# Revit family: Domotics-DomesticRanges-GEWISS-CHORUS_PROTECTION-ONE-WAY_SWITCH_MCB
name_source: partatom
category: Apparecchi elettrici
revit_build: Autodesk Revit 2016 (Build: 20161004_0715(x64)
units: mm (PartAtom-declared; Revit-internal decimal feet)

## family parameters
Condiviso = Sì
Host = Superficie
Mantenere orientamento annotazione = Sì
Punto di calcolo locali = Sì
Quota connettore circolare = Usa diametro
Taglio con vuoti quando caricato = Sì
Tipo di parte = Normale

## types (18) — shared parameters
Breaking capacity = 3KA
Carico apparente = 0 VA
Catalogue = DOMOTICS
Catalogue Range = CHORUS - DOMESTIC RANGE
Curve = C
Electrocod = 0131
IDF = 0539b41e-61ac-4be8-8c77-aad5fbf7d169
IDT = 300d05bc-7aec-4f69-9cb1-967f6c419845
Immagine tipo = GW14461.jpg
N. poli = 1
No. Chorus modules = 1
No. Chorus modules: = 1
Produttore = GEWISS S.p.A.
Prospetto di default = 1219 mm
SEO = MCB
Technical sheet = https://www.gewiss.com
Tipo_ = CHORUS INT MAGNETOTERMICO_GENERICO : TITANIO
Type = MCB
URL = https://www.gewiss.com
Version file RFA = 19.0
Volt = 230 V
Voltage = 230V ac
Voltage: = 230V ac

## per-type parameters (varying)
| type | Colour | Description. | Description: | Descrizione | EAN code | Modello | Rated current (A) | Rated current (In) |
| GW12462 - MCB 1P C10 3kA 230V ac 1M Black | Black | One-way switch (1P) | Single pole (1P) | MCB 1P C10 3KA 230V AC 1M BLACK | 8011564268166 | GW12462 | 10 | 10 |
| GW14463 - MCB 1P C16 3kA 230V ac 1M Titanium | Titanium | One-way switch (1P) | Single pole (1P) | MCB 1P C16 3KA 230V AC 1M TITAN | 8011564267725 | GW14463 | 16 | 16 |
| GW14466 - MCB 1P+N C6 3kA 230V ac 1M Titanium | Titanium | One-way switch (1P+N) | Two-pole (1P+N) | MCB 1P+N C6 3KA 230V AC 1M TITAN | 8011564267732 | GW14466 | 6 | 6 |
| GW10468 - MCB 1P+N C16 3kA 230V ac 1M White | White | One-way switch (1P+N) | Two-pole (1P+N) | MCB 1P+N C16 3KA 230V AC 1M W | 8011564262706 | GW10468 | 16 | 16 |
| GW10462 - MCB 1P C10 3kA 230V ac 1M White | White | One-way switch (1P) | Single pole (1P) | MCB 1P C10 3KA 230V AC 1M WHITE | 8011564262669 | GW10462 | 10 | 10 |
| GW14468 - MCB 1P+N C16 3kA 230V ac 1M Titanium | Titanium | One-way switch (1P+N) | Two-pole (1P+N) | MCB 1P+N C16 3KA 230V AC 1M W | 8011564267756 | GW14468 | 16 | 16 |
| GW10467 - MCB 1P+N C10 3kA 230V ac 1M White | White | One-way switch (1P+N) | Two-pole (1P+N) | MCB 1P+N C10 3KA 230V AC 1M W | 8011564262690 | GW10467 | 10 | 10 |
| GW12467 - MCB 1P+N C10 3kA 230V ac 1M Black | Black | One-way switch (1P+N) | Two-pole (1P+N) | MCB 1P+N C10 3KA 230V AC 1M W | 8011564268210 | GW12467 | 10 | 10 |
| GW14467 - MCB 1P+N C10 3kA 230V ac 1M Titanium | Titanium | One-way switch (1P+N) | Two-pole (1P+N) | MCB 1P+N C10 3KA 230V AC 1M W | 8011564267749 | GW14467 | 10 | 10 |
| GW14461 - MCB 1P C6 3kA 230V ac 1M Titanium | Titanium | One-way switch (1P) | Single pole (1P) | MCB 1P C6 3KA 230V AC 1M TITAN | 8011564265202 | GW14461 | 6 | 6 |
| GW12461 - MCB 1P C6 3kA 230V ac 1M Black | Black | One-way switch (1P) | Single pole (1P) | MCB 1P C6 3KA 230V AC 1M BLACK | 8011564268159 | GW12461 | 6 | 6 |
| GW12466 - MCB 1P+N C6 3kA 230V ac 1M Black | Black | One-way switch (1P+N) | Two-pole (1P+N) | MCB 1P+N C6 3KA 230V AC 1M BLACK | 8011564268197 | GW12466 | 6 | 6 |
| GW12468 - MCB 1P+N C16 3kA 230V ac 1M Black | Black | One-way switch (1P+N) | Two-pole (1P+N) | MCB 1P+N C16 3KA 230V AC 1M W | 8011564268227 | GW12468 | 16 | 16 |
| GW12463 - MCB 1P C16 3kA 230V ac 1M Black | Black | One-way switch (1P) | Single pole (1P) | MCB 1P C16 3KA 230V AC 1M BLACK | 8011564268180 | GW12463 | 16 | 16 |
| GW10461 - MCB 1P C6 3kA 230V ac 1M White | White | One-way switch (1P) | Single pole (1P) | MCB 1P C6 3KA 230V AC 1M WHITE | 8011564262652 | GW10461 | 6 | 6 |
| GW10463 - MCB 1P C16 3kA 230V ac 1M White | White | One-way switch (1P) | Single pole (1P) | MCB 1P C16 3KA 230V AC 1M WHITE | 8011564262676 | GW10463 | 16 | 16 |
| GW14462 - MCB 1P C10 3kA 230V ac 1M Titanium | Titanium | One-way switch (1P) | Single pole (1P) | MCB 1P C10 3KA 230V AC 1M TITAN | 8011564267718 | GW14462 | 10 | 10 |
| GW10466 - MCB 1P+N C6 3kA 230V ac 1M White | White | One-way switch (1P+N) | Two-pole (1P+N) | MCB 1P+N C6 3KA 230V AC 1M WHITE | 8011564262683 | GW10466 | 6 | 6 |

## geometry (parser evidence)
native form markers: Sweep x2
no freeform markers — native parametric forms only
